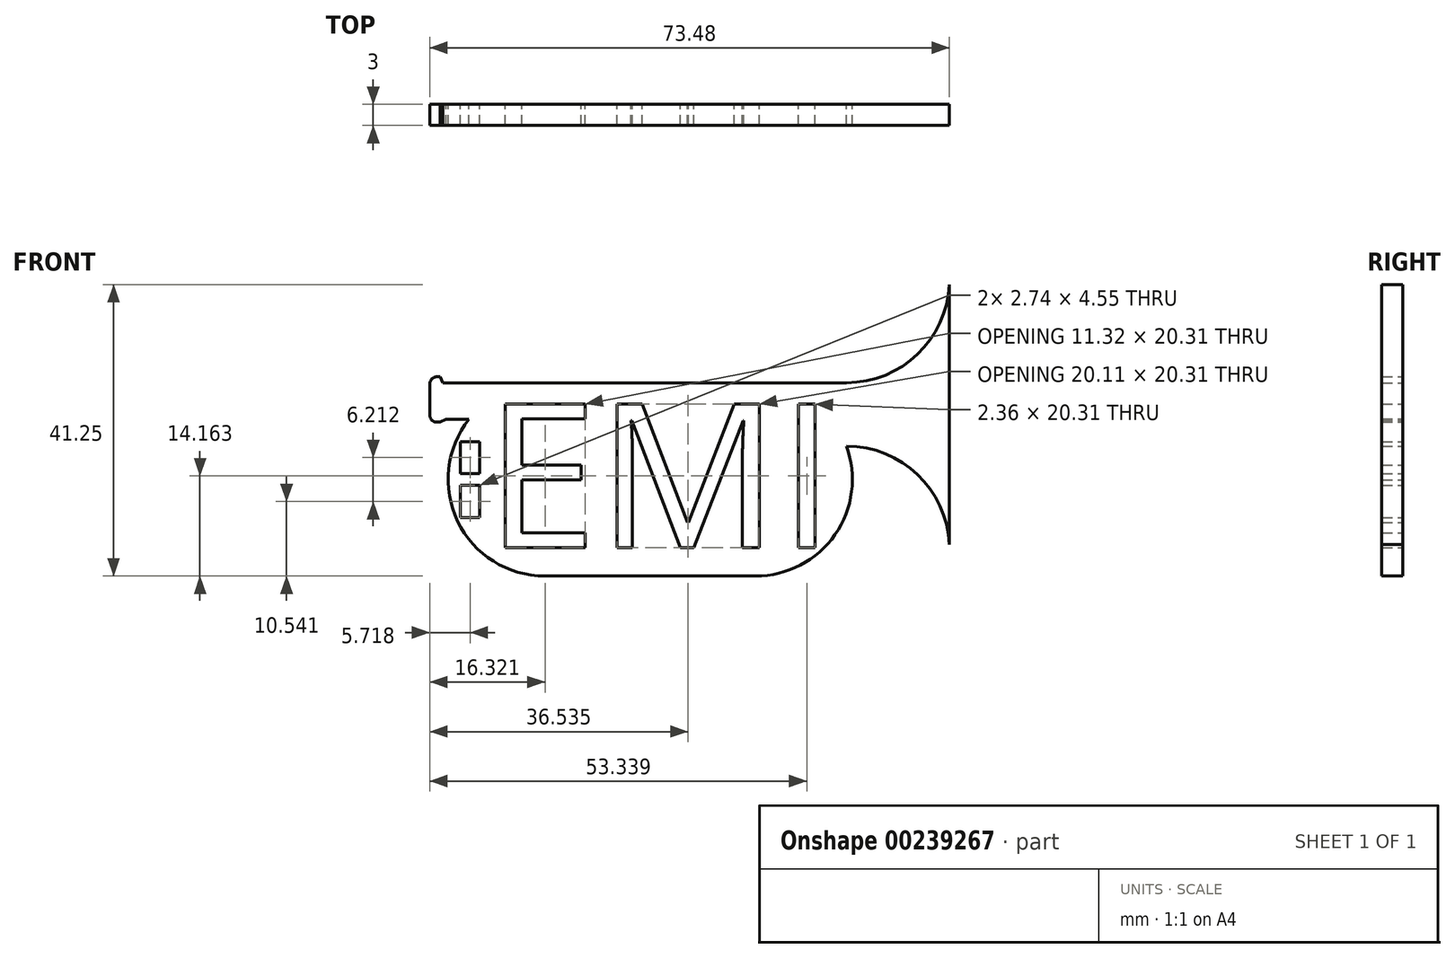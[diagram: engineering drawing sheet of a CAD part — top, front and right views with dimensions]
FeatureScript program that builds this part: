
annotation { "Feature Type Name" : "Feature", "Feature Type Description" : "" }
export const myFeature = defineFeature(function(context is Context, id is Id, definition is map)
    precondition{}
    {
        {
            var Q0;
            Q0=qCreatedBy(makeId("Front.planeOp"),FACE);
            var sketch = newSketch(context, id + "F0", { "sketchPlane" : qUnion([Q0])});
            skArc(sketch, "E0", {"start": v(-10.7, 8.5) * mm, "mid": v(-12.3, -5.95) * mm, "end": v(0, -13.67) * mm});
            skArc(sketch, "E1", {"start": v(29.83, -13.67) * mm, "mid": v(41.04, -7.82) * mm, "end": v(42.66, 4.72) * mm});
            skLineSegment(sketch, "E2", {"start": v(0, 13.67) * mm, "end": v(29.83, 13.67) * mm});
            skLineSegment(sketch, "E3", {"start": v(0, -13.67) * mm, "end": v(29.83, -13.67) * mm});
            skLineSegment(sketch, "E4", {"start": v(0, 13.67) * mm, "end": v(-14.43, 13.67) * mm});
            skLineSegment(sketch, "E5", {"start": v(-14.43, 13.67) * mm, "end": v(-14.83, 14.51) * mm});
            skLineSegment(sketch, "E6", {"start": v(-14.83, 14.51) * mm, "end": v(-15.27, 14.51) * mm});
            skLineSegment(sketch, "E7", {"start": v(-16.27, 13.51) * mm, "end": v(-16.27, 9.1) * mm});
            skLineSegment(sketch, "E8", {"start": v(-15.27, 8.1) * mm, "end": v(-14.83, 8.1) * mm});
            skLineSegment(sketch, "E9", {"start": v(-14.83, 8.1) * mm, "end": v(-13.99, 8.5) * mm});
            skLineSegment(sketch, "E10", {"start": v(-13.99, 8.5) * mm, "end": v(-10.7, 8.5) * mm});
            skPoint(sketch, "E11.visualSharp", {"position": v(-16.27, 14.51) * mm});
            skArc(sketch, "E11.filletArc", {"start": v(-15.27, 14.51) * mm, "mid": v(-15.98, 14.22) * mm, "end": v(-16.27, 13.51) * mm});
            skPoint(sketch, "E12.visualSharp", {"position": v(-16.27, 8.1) * mm});
            skArc(sketch, "E12.filletArc", {"start": v(-16.27, 9.1) * mm, "mid": v(-15.98, 8.4) * mm, "end": v(-15.27, 8.1) * mm});
            skLineSegment(sketch, "E13", {"start": v(29.83, 13.67) * mm, "end": v(42.66, 13.67) * mm});
            skLineSegment(sketch, "E14", {"start": v(42.66, 4.72) * mm, "end": v(42.66, 4.72) * mm});
            skLineSegment(sketch, "E15", {"start": v(42.66, 13.67) * mm, "end": v(42.66, 4.72) * mm, "construction": true});
            skArc(sketch, "E16", {"start": v(42.66, 13.67) * mm, "mid": v(53.19, 18.17) * mm, "end": v(57.21, 28.88) * mm});
            skArc(sketch, "E17", {"start": v(57.21, -9.2) * mm, "mid": v(52.73, 0.68) * mm, "end": v(42.66, 4.72) * mm});
            skLineSegment(sketch, "E18", {"start": v(42.66, 28.23) * mm, "end": v(42.66, -9.84) * mm, "construction": true});
            skLineSegment(sketch, "E19", {"start": v(57.21, 28.88) * mm, "end": v(57.21, -9.2) * mm});
            skLineSegment(sketch, "E20.bottom", {"start": v(-11.92, 5.36) * mm, "end": v(-9.18, 5.36) * mm});
            skLineSegment(sketch, "E20.top", {"start": v(-11.92, -5.4) * mm, "end": v(-9.18, -5.4) * mm});
            skLineSegment(sketch, "E20.left", {"start": v(-11.92, 5.36) * mm, "end": v(-11.92, 0.8) * mm});
            skLineSegment(sketch, "E20.right", {"start": v(-9.18, 5.36) * mm, "end": v(-9.18, 0.8) * mm});
            skPoint(sketch, "E21.endSnap0", {"position": v(-9.18, -0.02) * mm});
            skLineSegment(sketch, "E22.trimOffspring", {"start": v(-11.92, -0.86) * mm, "end": v(-11.92, -5.4) * mm});
            skLineSegment(sketch, "E23.trimOffspring", {"start": v(-9.18, -0.86) * mm, "end": v(-9.18, -5.4) * mm});
            skLineSegment(sketch, "E24", {"start": v(-11.92, 0.8) * mm, "end": v(-9.18, 0.8) * mm});
            skLineSegment(sketch, "E25", {"start": v(-11.92, -0.86) * mm, "end": v(-9.18, -0.86) * mm});
            skPoint(sketch, "E26.orphan", {"position": v(-9.18, 0) * mm});
            skPoint(sketch, "E27.orphan", {"position": v(-11.92, -0.02) * mm});
            skText(sketch, "E28", { "text": "EMI\n", "fontName": "OpenSans-Regular.ttf"});
            const initialGuessF0  = {"E28": [-0.0084, -0.00966, 1, 0, 0.02048]};
            skSetInitialGuess(sketch, initialGuessF0);
            skSolve(sketch);
        }
        {
            var Q0;
            Q0=makeQuery(id+"F0.imprint","IMPRINT",FACE,{"disambiguationData":[TD([[makeQuery(id+"F0.imprint","IMPRINT",EDGE,{"derivedFrom":sQuery(id+"F0.wireOp",EDGE,"E0")}),1.0]])]});
            extrude(context, id + "F1", {"entities" : qUnion([Q0]), "depth" : 3 * mm});
        }
    });
